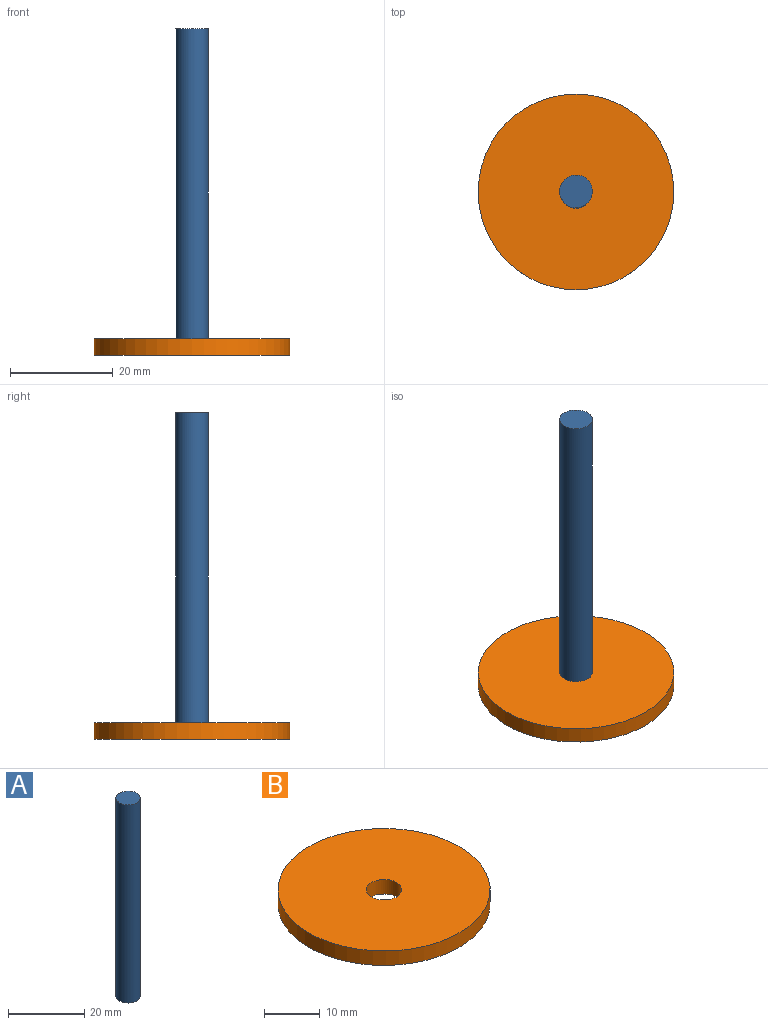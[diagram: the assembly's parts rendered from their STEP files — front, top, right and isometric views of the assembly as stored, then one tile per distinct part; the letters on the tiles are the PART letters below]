
ASSEMBLY  parts=2 mates=1
PART A: 3 faces, bbox 6.4x6.4x63.5 mm
  f0: plane 6.35x6.35mm, normal (0,0,1), area 31.7mm2, adj f1
  f1: cylinder r=3.17mm len=63.5mm, axis (0,0,-1), area 1266.8mm2, adj f0,f2
  f2: plane 6.35x6.35mm, normal (0,0,-1), area 31.7mm2, adj f1
PART B: 4 faces, bbox 38.1x38.1x3.2 mm
  f0: cylinder r=3.17mm len=6.35mm, axis (0,0,-1), area 63.3mm2, adj f2,f3
  f1: cylinder r=19.05mm len=38.1mm, axis (0,0,-1), area 380mm2, adj f2,f3
  f2: plane 38.1x38.1mm, normal (0,0,1), area 1108.4mm2, adj f0,f1
  f3: plane 38.1x38.1mm, normal (0,0,-1), area 1108.4mm2, adj f0,f1
PLACE A t=(69.85,0,-69.85)mm
PLACE B rot(axis=(0,0,-1),90deg) t=(0,-69.85,-69.85)mm
MATE fastened A.f1 <-> B.f1  axis (0,0,-1) through (0,0,0)mm
